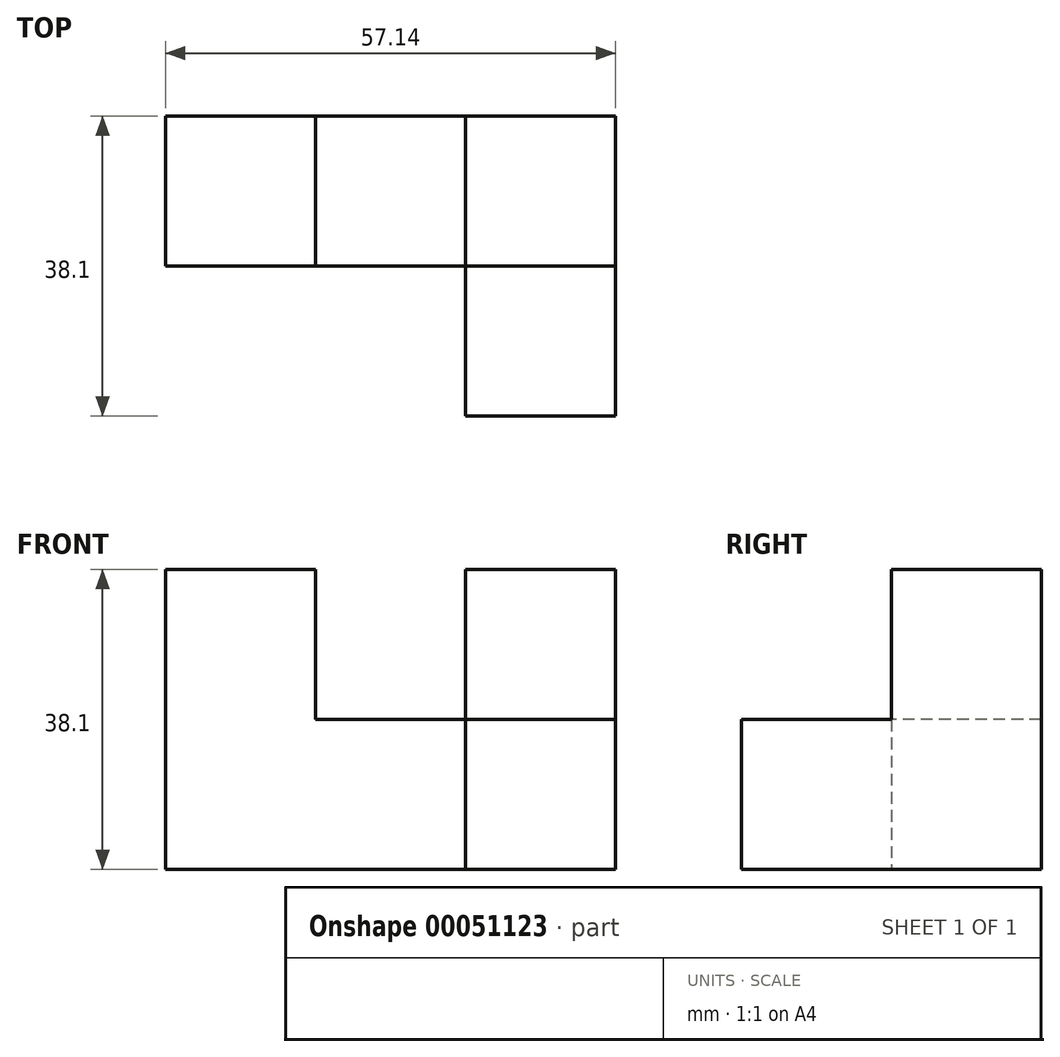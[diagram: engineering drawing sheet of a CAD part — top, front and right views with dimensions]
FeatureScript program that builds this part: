
annotation { "Feature Type Name" : "Feature", "Feature Type Description" : "" }
export const myFeature = defineFeature(function(context is Context, id is Id, definition is map)
    precondition{}
    {
        {
            var Q0;
            Q0=qCreatedBy(makeId("Top.planeOp"),FACE);
            var sketch = newSketch(context, id + "F0", { "sketchPlane" : qUnion([Q0])});
            skLineSegment(sketch, "E0.rect.bottom", {"start": v(-28.57, 9.53) * mm, "end": v(28.58, 9.53) * mm});
            skLineSegment(sketch, "E0.rect.top", {"start": v(-28.58, -9.53) * mm, "end": v(28.57, -9.53) * mm});
            skLineSegment(sketch, "E0.rect.left", {"start": v(-28.58, 9.53) * mm, "end": v(-28.58, -9.53) * mm});
            skLineSegment(sketch, "E0.rect.right", {"start": v(28.58, 9.53) * mm, "end": v(28.57, -9.53) * mm});
            skPoint(sketch, "E0.rect.middle", {"position": v(0, 0) * mm});
            skSolve(sketch);
        }
        {
            var Q0;
            Q0 = qSketchRegion(id + "F0", true);
            extrude(context, id + "F1", {"entities" : qUnion([Q0]), "depth" : 19.05 * mm});
        }
        {
            var Q0;
            Q0=makeQuery(id+"F1.opExtrude","CAP_FACE",FACE,{"disambiguationData":[OSD([sQuery(id+"F0.wireOp",EDGE,"E0.rect.bottom"),sQuery(id+"F0.wireOp",EDGE,"E0.rect.top"),sQuery(id+"F0.wireOp",EDGE,"E0.rect.left"),sQuery(id+"F0.wireOp",EDGE,"E0.rect.right")])],"isStart":false});
            var sketch = newSketch(context, id + "F2", { "sketchPlane" : qUnion([Q0])});
            skLineSegment(sketch, "E1.bottom", {"start": v(-28.58, 9.53) * mm, "end": v(-9.53, 9.53) * mm});
            skLineSegment(sketch, "E1.top", {"start": v(-28.58, -9.53) * mm, "end": v(-9.53, -9.53) * mm});
            skLineSegment(sketch, "E1.left", {"start": v(-28.58, 9.53) * mm, "end": v(-28.58, -9.53) * mm});
            skLineSegment(sketch, "E1.right", {"start": v(-9.53, 9.53) * mm, "end": v(-9.53, -9.53) * mm});
            skLineSegment(sketch, "E2.bottom", {"start": v(28.58, 9.53) * mm, "end": v(9.53, 9.53) * mm});
            skLineSegment(sketch, "E2.top", {"start": v(28.58, -9.53) * mm, "end": v(9.53, -9.53) * mm});
            skLineSegment(sketch, "E2.left", {"start": v(28.58, 9.53) * mm, "end": v(28.58, -9.53) * mm});
            skLineSegment(sketch, "E2.right", {"start": v(9.53, 9.53) * mm, "end": v(9.53, -9.53) * mm});
            skSolve(sketch);
        }
        {
            var Q0;
            Q0=makeQuery(id+"F2.imprint","IMPRINT",FACE,{"disambiguationData":[TD([[makeQuery(id+"F2.imprint","IMPRINT",EDGE,{"derivedFrom":sQuery(id+"F2.wireOp",EDGE,"E1.bottom")}),-1.0]])]});
            var Q1;
            Q1=makeQuery(id+"F2.imprint","IMPRINT",FACE,{"disambiguationData":[TD([[makeQuery(id+"F2.imprint","IMPRINT",EDGE,{"derivedFrom":sQuery(id+"F2.wireOp",EDGE,"E2.bottom")}),-1.0]])]});
            extrude(context, id + "F3", {"entities" : qUnion([Q0, Q1]), "operationType" : NewBodyOperationType.ADD, "depth" : 19.05 * mm});
        }
        {
            var Q0;
            Q0=makeQuery(id+"F3.boolean.opBoolean","MERGE",FACE,{"derivedFrom":[makeQuery(id+"F1.opExtrude","SWEPT_FACE",FACE,{"disambiguationData":[OSD([sQuery(id+"F0.wireOp",EDGE,"E0.rect.top")])]}),makeQuery(id+"F3.opExtrude","SWEPT_FACE",FACE,{"disambiguationData":[OSD([sQuery(id+"F2.wireOp",EDGE,"E1.top")])]}),makeQuery(id+"F3.opExtrude","SWEPT_FACE",FACE,{"disambiguationData":[OSD([sQuery(id+"F2.wireOp",EDGE,"E2.top")])]})]});
            var sketch = newSketch(context, id + "F4", { "sketchPlane" : qUnion([Q0])});
            skLineSegment(sketch, "E3.bottom", {"start": v(-28.58, 0) * mm, "end": v(-9.53, 0) * mm});
            skLineSegment(sketch, "E3.top", {"start": v(-28.58, 19.05) * mm, "end": v(-9.53, 19.05) * mm});
            skLineSegment(sketch, "E3.left", {"start": v(-28.58, 0) * mm, "end": v(-28.58, 19.05) * mm});
            skLineSegment(sketch, "E3.right", {"start": v(-9.53, 0) * mm, "end": v(-9.53, 19.05) * mm});
            skLineSegment(sketch, "E4.bottom", {"start": v(9.53, 19.05) * mm, "end": v(28.57, 19.05) * mm});
            skLineSegment(sketch, "E4.top", {"start": v(9.53, 0) * mm, "end": v(28.57, 0) * mm});
            skLineSegment(sketch, "E4.left", {"start": v(9.53, 19.05) * mm, "end": v(9.53, 0) * mm});
            skLineSegment(sketch, "E4.right", {"start": v(28.57, 19.05) * mm, "end": v(28.57, 0) * mm});
            skSolve(sketch);
        }
        {
            var Q0;
            Q0=makeQuery(id+"F4.imprint","IMPRINT",FACE,{"disambiguationData":[TD([[makeQuery(id+"F4.imprint","IMPRINT",EDGE,{"derivedFrom":sQuery(id+"F4.wireOp",EDGE,"E4.bottom")}),-1.0]])]});
            extrude(context, id + "F5", {"entities" : qUnion([Q0]), "operationType" : NewBodyOperationType.ADD, "depth" : 19.05 * mm});
        }
    });
